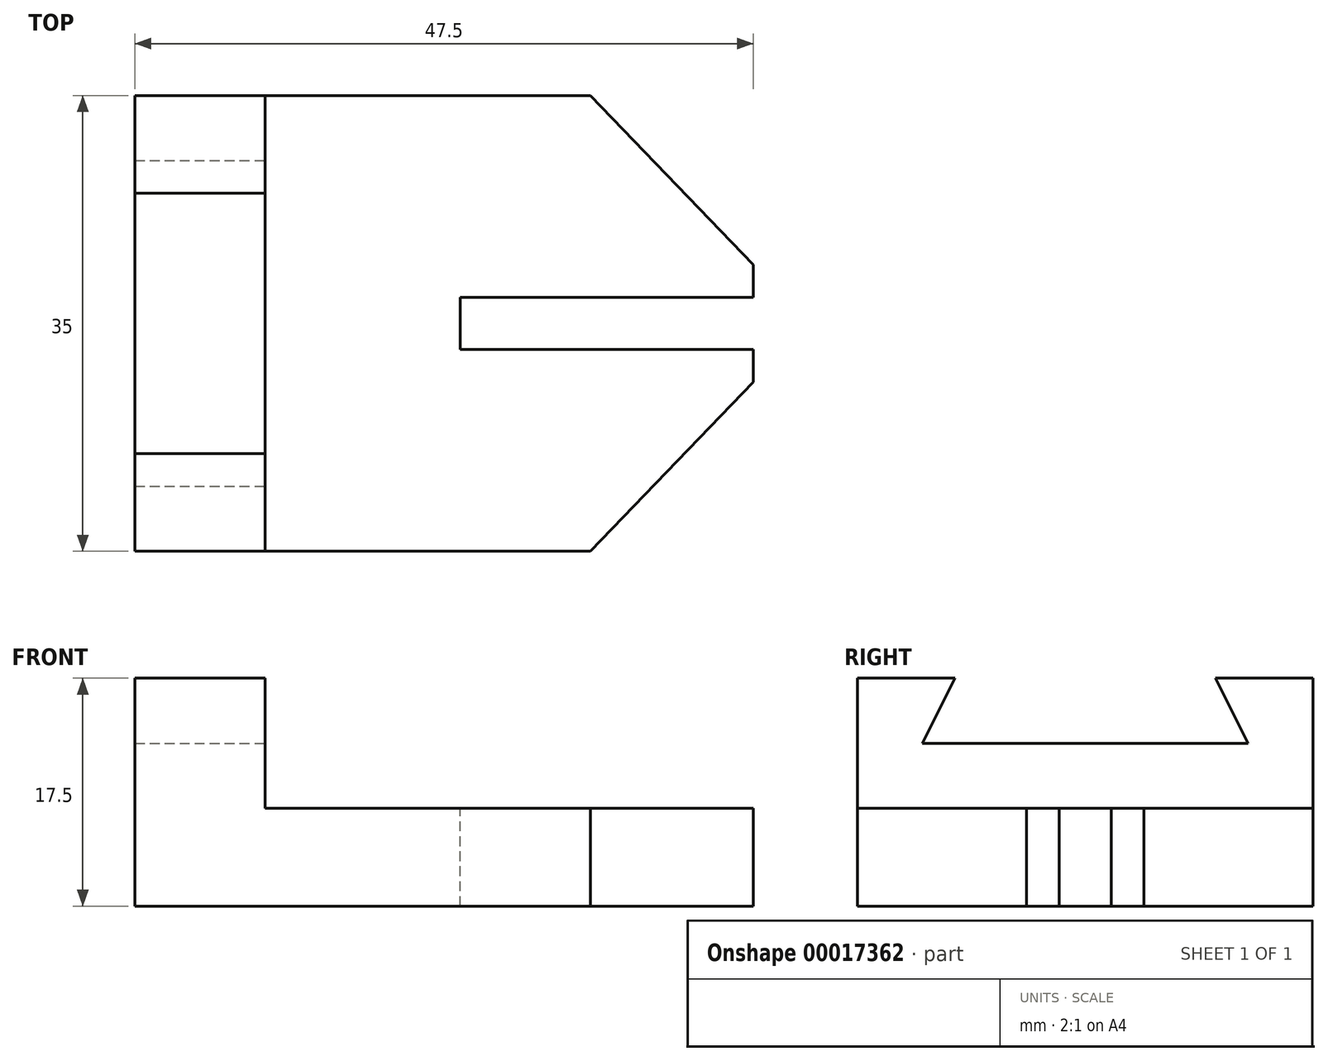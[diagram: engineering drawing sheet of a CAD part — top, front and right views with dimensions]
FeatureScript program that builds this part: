
annotation { "Feature Type Name" : "Feature", "Feature Type Description" : "" }
export const myFeature = defineFeature(function(context is Context, id is Id, definition is map)
    precondition{}
    {
        {
            var Q0;
            Q0=qCreatedBy(makeId("Front.planeOp"),FACE);
            var sketch = newSketch(context, id + "F0", { "sketchPlane" : qUnion([Q0])});
            skLineSegment(sketch, "E0.bottom", {"start": v(-23.46, 4.02) * mm, "end": v(24.04, 4.02) * mm});
            skLineSegment(sketch, "E0.top", {"start": v(-23.46, -3.48) * mm, "end": v(24.04, -3.48) * mm});
            skLineSegment(sketch, "E0.left", {"start": v(-23.46, 4.02) * mm, "end": v(-23.46, -3.48) * mm});
            skLineSegment(sketch, "E0.right", {"start": v(24.04, 4.02) * mm, "end": v(24.04, -3.48) * mm});
            skSolve(sketch);
        }
        {
            var Q0;
            Q0=makeQuery(id+"F0.imprint","IMPRINT",FACE,{"disambiguationData":[TD([[makeQuery(id+"F0.imprint","IMPRINT",EDGE,{"derivedFrom":sQuery(id+"F0.wireOp",EDGE,"E0.bottom")}),-1.0]])]});
            extrude(context, id + "F1", {"entities" : qUnion([Q0]), "depth" : 35 * mm});
        }
        {
            var Q0;
            Q0=makeQuery(id+"F1.opExtrude","SWEPT_FACE",FACE,{"disambiguationData":[OSD([sQuery(id+"F0.wireOp",EDGE,"E0.bottom")])]});
            var sketch = newSketch(context, id + "F2", { "sketchPlane" : qUnion([Q0])});
            skLineSegment(sketch, "E1.bottom", {"start": v(-23.46, 0) * mm, "end": v(-13.46, 0) * mm});
            skLineSegment(sketch, "E1.top", {"start": v(-23.46, -35) * mm, "end": v(-13.46, -35) * mm});
            skLineSegment(sketch, "E1.left", {"start": v(-23.46, 0) * mm, "end": v(-23.46, -35) * mm});
            skLineSegment(sketch, "E1.right", {"start": v(-13.46, 0) * mm, "end": v(-13.46, -35) * mm});
            skLineSegment(sketch, "E2", {"start": v(24.04, 0) * mm, "end": v(11.54, 0) * mm});
            skLineSegment(sketch, "E3", {"start": v(24.04, 0) * mm, "end": v(24.04, -13) * mm});
            skLineSegment(sketch, "E4", {"start": v(24.04, -13) * mm, "end": v(11.54, 0) * mm});
            skLineSegment(sketch, "E5", {"start": v(24.04, -22) * mm, "end": v(24.04, -35) * mm});
            skLineSegment(sketch, "E6", {"start": v(24.04, -35) * mm, "end": v(11.54, -35) * mm});
            skLineSegment(sketch, "E7", {"start": v(11.54, -35) * mm, "end": v(24.04, -22) * mm});
            skSolve(sketch);
        }
        {
            var Q0;
            Q0=makeQuery(id+"F2.imprint","IMPRINT",FACE,{"disambiguationData":[TD([[makeQuery(id+"F2.imprint","IMPRINT",EDGE,{"derivedFrom":sQuery(id+"F2.wireOp",EDGE,"E5")}),1.0]])]});
            extrude(context, id + "F3", {"entities" : qUnion([Q0]), "operationType" : NewBodyOperationType.REMOVE, "oppositeDirection" : true, "depth" : 25 * mm});
        }
        {
            var Q0;
            Q0=makeQuery(id+"F2.imprint","IMPRINT",FACE,{"disambiguationData":[TD([[makeQuery(id+"F2.imprint","IMPRINT",EDGE,{"derivedFrom":sQuery(id+"F2.wireOp",EDGE,"E2")}),-1.0]])]});
            extrude(context, id + "F4", {"entities" : qUnion([Q0]), "operationType" : NewBodyOperationType.REMOVE, "oppositeDirection" : true, "depth" : 25 * mm});
        }
        {
            var Q0;
            Q0=makeQuery(id+"F2.imprint","IMPRINT",FACE,{"disambiguationData":[TD([[makeQuery(id+"F2.imprint","IMPRINT",EDGE,{"derivedFrom":sQuery(id+"F2.wireOp",EDGE,"E1.bottom")}),-1.0]])]});
            extrude(context, id + "F5", {"entities" : qUnion([Q0]), "operationType" : NewBodyOperationType.ADD, "depth" : 10 * mm});
        }
        {
            var Q0;
            Q0=makeQuery(id+"F1.opExtrude","SWEPT_FACE",FACE,{"disambiguationData":[OSD([sQuery(id+"F0.wireOp",EDGE,"E0.bottom")])]});
            var sketch = newSketch(context, id + "F6", { "sketchPlane" : qUnion([Q0])});
            skLineSegment(sketch, "E8", {"start": v(24.04, -13) * mm, "end": v(24.04, -15.5) * mm});
            skLineSegment(sketch, "E9", {"start": v(24.04, -22) * mm, "end": v(24.04, -19.5) * mm});
            skLineSegment(sketch, "E10", {"start": v(24.04, -15.5) * mm, "end": v(1.54, -15.5) * mm});
            skLineSegment(sketch, "E11", {"start": v(24.04, -19.5) * mm, "end": v(1.54, -19.5) * mm});
            skLineSegment(sketch, "E12", {"start": v(1.54, -19.5) * mm, "end": v(1.54, -15.5) * mm});
            skSolve(sketch);
        }
        {
            var Q0;
            {var subQ2=sQuery(id+"F6.wireOp",EDGE,"E10");Q0=makeQuery(id+"F6.imprint","IMPRINT",FACE,{"disambiguationData":[TD([[makeQuery(id+"F6.imprint","IMPRINT",EDGE,{"derivedFrom":subQ2}),1.0]])]});}
            extrude(context, id + "F7", {"entities" : qUnion([Q0]), "operationType" : NewBodyOperationType.REMOVE, "oppositeDirection" : true, "depth" : 25 * mm});
        }
        {
            var Q0;
            Q0=makeQuery(id+"F5.opExtrude","SWEPT_FACE",FACE,{"disambiguationData":[OSD([sQuery(id+"F2.wireOp",EDGE,"E1.right")])]});
            var sketch = newSketch(context, id + "F8", { "sketchPlane" : qUnion([Q0])});
            skLineSegment(sketch, "E13", {"start": v(-35, 14.02) * mm, "end": v(-27.5, 14.02) * mm});
            skLineSegment(sketch, "E14", {"start": v(0, 14.02) * mm, "end": v(-7.5, 14.02) * mm});
            skLineSegment(sketch, "E15", {"start": v(-27.5, 14.02) * mm, "end": v(-30, 9.02) * mm});
            skLineSegment(sketch, "E16", {"start": v(-7.5, 14.02) * mm, "end": v(-5, 9.02) * mm});
            skLineSegment(sketch, "E17", {"start": v(-30, 9.02) * mm, "end": v(-5, 9.02) * mm});
            skLineSegment(sketch, "E18", {"start": v(-27.5, 14.02) * mm, "end": v(-7.5, 14.02) * mm});
            skSolve(sketch);
        }
        {
            var Q0;
            Q0=makeQuery(id+"F8.imprint","IMPRINT",FACE,{"disambiguationData":[TD([[makeQuery(id+"F8.imprint","IMPRINT",EDGE,{"derivedFrom":sQuery(id+"F8.wireOp",EDGE,"E15")}),1.0]])]});
            extrude(context, id + "F9", {"entities" : qUnion([Q0]), "operationType" : NewBodyOperationType.REMOVE, "oppositeDirection" : true, "depth" : 25 * mm});
        }
    });
